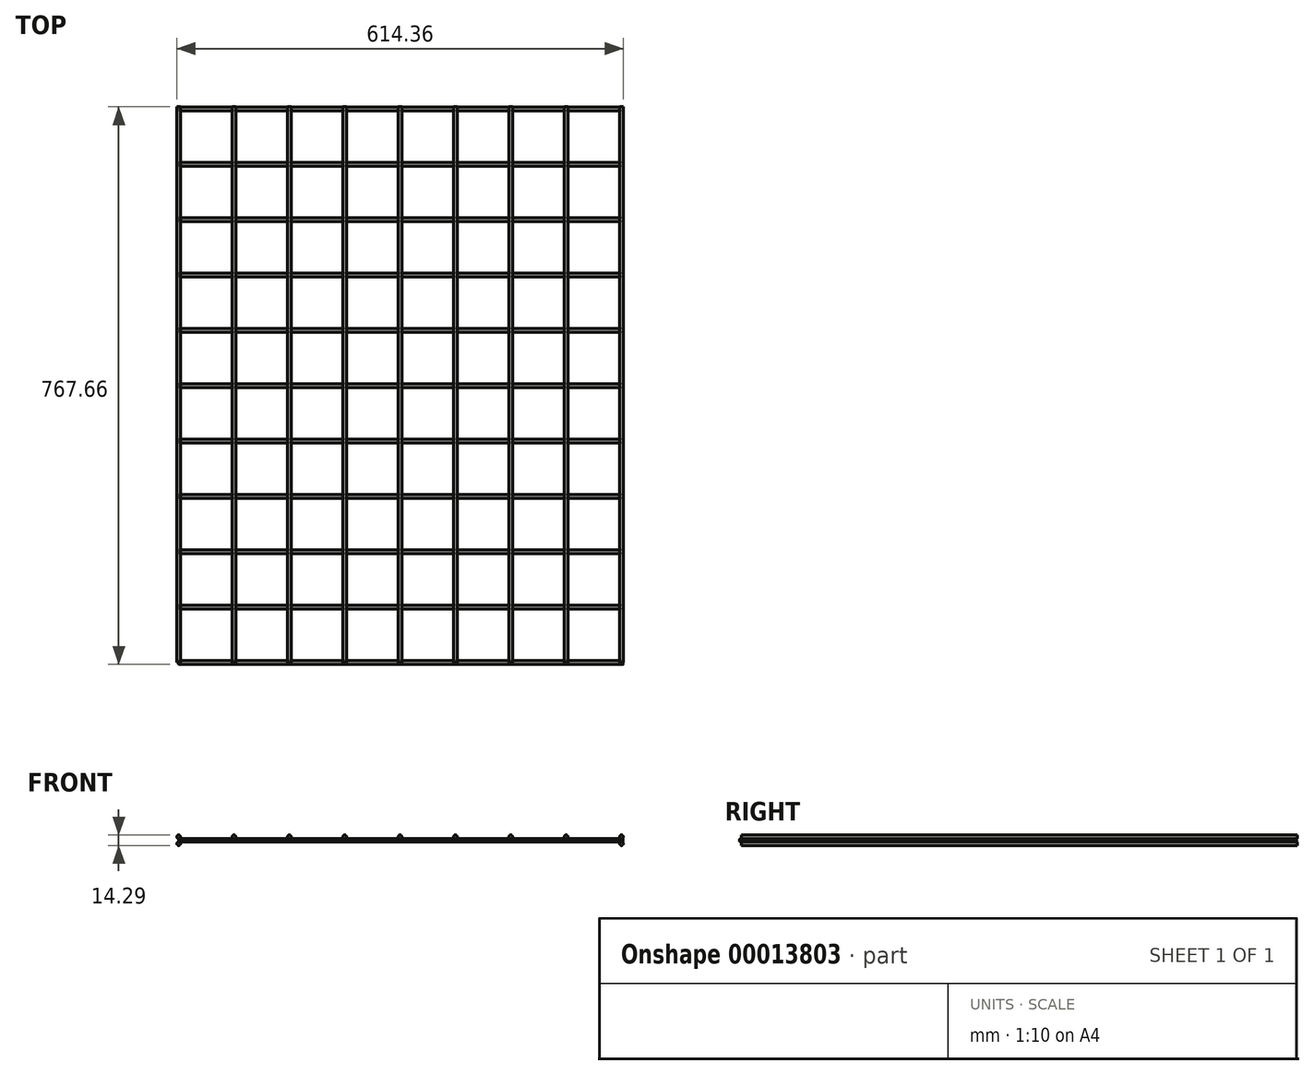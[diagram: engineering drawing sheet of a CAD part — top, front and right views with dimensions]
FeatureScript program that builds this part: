
annotation { "Feature Type Name" : "Feature", "Feature Type Description" : "" }
export const myFeature = defineFeature(function(context is Context, id is Id, definition is map)
    precondition{}
    {
        {
            var Q0;
            Q0=qCreatedBy(makeId("Front.planeOp"),FACE);
            var sketch = newSketch(context, id + "F0", { "sketchPlane" : qUnion([Q0])});
            skCircle(sketch, "E0", {"center": v(0, 0) * mm, "radius": 2.38 * mm});
            skCircle(sketch, "E1.1.0.0", {"center": v(76.2, 0) * mm, "radius": 2.38 * mm});
            skCircle(sketch, "E1.2.0.0", {"center": v(152.4, 0) * mm, "radius": 2.38 * mm});
            skCircle(sketch, "E1.3.0.0", {"center": v(228.6, 0) * mm, "radius": 2.38 * mm});
            skCircle(sketch, "E1.4.0.0", {"center": v(304.8, 0) * mm, "radius": 2.38 * mm});
            skCircle(sketch, "E1.5.0.0", {"center": v(381, 0) * mm, "radius": 2.38 * mm});
            skCircle(sketch, "E1.6.0.0", {"center": v(457.2, 0) * mm, "radius": 2.38 * mm});
            skLineSegment(sketch, "E1.direction1", {"start": v(0, 0) * mm, "end": v(76.2, 0) * mm, "construction": true});
            skCircle(sketch, "E2.0.7.0", {"center": v(533.4, 0) * mm, "radius": 2.38 * mm});
            skCircle(sketch, "E2.0.8.0", {"center": v(609.6, 0) * mm, "radius": 2.38 * mm});
            skCircle(sketch, "E3", {"center": v(0, -9.53) * mm, "radius": 2.38 * mm});
            skCircle(sketch, "E4.1.0.0", {"center": v(609.6, -9.53) * mm, "radius": 2.38 * mm});
            skLineSegment(sketch, "E4.direction1", {"start": v(0, -9.53) * mm, "end": v(609.6, -9.53) * mm, "construction": true});
            skSolve(sketch);
        }
        {
            var Q0;
            Q0 = qSketchRegion(id + "F0", true);
            extrude(context, id + "F1", {"entities" : qUnion([Q0]), "oppositeDirection" : true, "depth" : 765.17 * mm});
        }
        {
            var Q0;
            Q0=qCreatedBy(makeId("Right.planeOp"),FACE);
            var sketch = newSketch(context, id + "F2", { "sketchPlane" : qUnion([Q0])});
            skCircle(sketch, "E5", {"center": v(0, -4.76) * mm, "radius": 2.48 * mm});
            skCircle(sketch, "E6.1.0.0", {"center": v(76.2, -4.76) * mm, "radius": 2.48 * mm});
            skCircle(sketch, "E6.2.0.0", {"center": v(152.4, -4.76) * mm, "radius": 2.48 * mm});
            skCircle(sketch, "E6.3.0.0", {"center": v(228.6, -4.76) * mm, "radius": 2.48 * mm});
            skCircle(sketch, "E6.4.0.0", {"center": v(304.8, -4.76) * mm, "radius": 2.48 * mm});
            skCircle(sketch, "E6.5.0.0", {"center": v(381, -4.76) * mm, "radius": 2.48 * mm});
            skCircle(sketch, "E6.6.0.0", {"center": v(457.2, -4.76) * mm, "radius": 2.48 * mm});
            skCircle(sketch, "E6.7.0.0", {"center": v(533.4, -4.76) * mm, "radius": 2.48 * mm});
            skCircle(sketch, "E6.8.0.0", {"center": v(609.6, -4.76) * mm, "radius": 2.48 * mm});
            skLineSegment(sketch, "E6.direction1", {"start": v(0, -4.76) * mm, "end": v(76.2, -4.76) * mm, "construction": true});
            skCircle(sketch, "E7.0.9.0", {"center": v(685.8, -4.76) * mm, "radius": 2.48 * mm});
            skCircle(sketch, "E7.0.10.0", {"center": v(762, -4.76) * mm, "radius": 2.48 * mm});
            skSolve(sketch);
        }
        {
            var Q0;
            Q0 = qSketchRegion(id + "F2", true);
            extrude(context, id + "F3", {"entities" : qUnion([Q0]), "depth" : 611.63 * mm, "hasSecondDirection" : true, "secondDirectionOppositeDirection" : true, "secondDirectionDepth" : 1 / 406.4 * mm});
        }
    });
